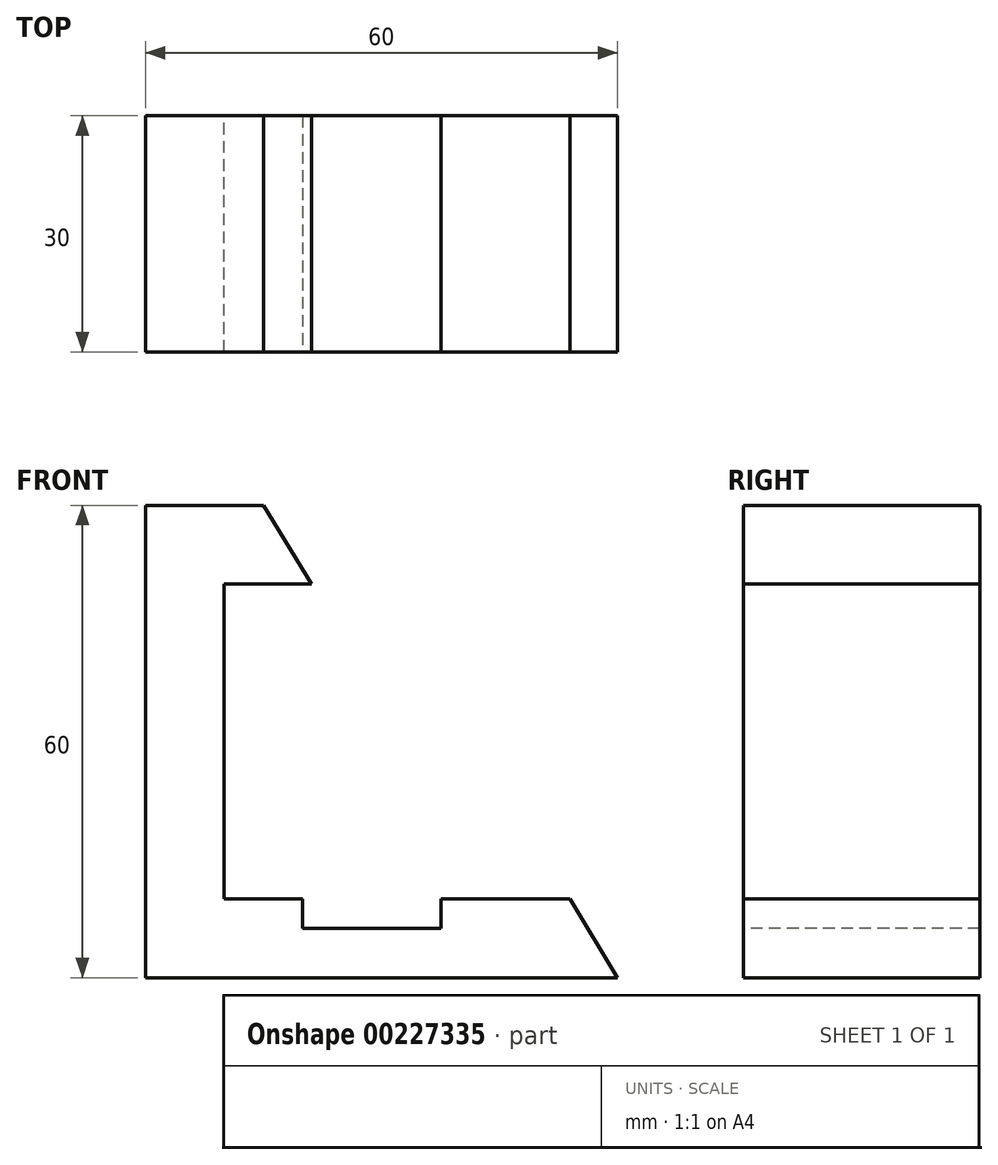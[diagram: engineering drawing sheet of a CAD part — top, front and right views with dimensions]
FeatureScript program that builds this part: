
annotation { "Feature Type Name" : "Feature", "Feature Type Description" : "" }
export const myFeature = defineFeature(function(context is Context, id is Id, definition is map)
    precondition{}
    {
        {
            var Q0;
            Q0=qCreatedBy(makeId("Front.planeOp"),FACE);
            var sketch = newSketch(context, id + "F0", { "sketchPlane" : qUnion([Q0])});
            skLineSegment(sketch, "E0", {"start": v(-68.5, -18.42) * mm, "end": v(-53.5, -18.42) * mm});
            skLineSegment(sketch, "E1", {"start": v(-68.5, -18.42) * mm, "end": v(-68.5, -78.42) * mm});
            skLineSegment(sketch, "E2", {"start": v(-68.5, -78.42) * mm, "end": v(-8.5, -78.42) * mm});
            skPoint(sketch, "E3", {"position": v(-68.5, -40.58) * mm});
            skPoint(sketch, "E4", {"position": v(-58.5, -28.42) * mm});
            skPoint(sketch, "E5", {"position": v(-58.5, -40.48) * mm});
            skLineSegment(sketch, "E6", {"start": v(-58.5, -28.42) * mm, "end": v(-58.5, -40.48) * mm});
            skPoint(sketch, "E7", {"position": v(-58.5, -78.42) * mm});
            skLineSegment(sketch, "E8", {"start": v(-53.5, -18.42) * mm, "end": v(-47.42, -28.42) * mm});
            skLineSegment(sketch, "E9", {"start": v(-58.5, -28.42) * mm, "end": v(-47.42, -28.42) * mm});
            skLineSegment(sketch, "E10", {"start": v(-8.5, -78.42) * mm, "end": v(-14.59, -68.42) * mm});
            skLineSegment(sketch, "E11", {"start": v(-14.59, -68.42) * mm, "end": v(-58.5, -68.42) * mm});
            skLineSegment(sketch, "E12", {"start": v(-58.5, -40.48) * mm, "end": v(-58.5, -68.42) * mm});
            skLineSegment(sketch, "E13", {"start": v(-80, 60) * mm, "end": v(-80, 0) * mm});
            skLineSegment(sketch, "E14", {"start": v(-80, 0) * mm, "end": v(0, 0) * mm});
            skLineSegment(sketch, "E15", {"start": v(-80, 60) * mm, "end": v(-50, 60) * mm});
            skLineSegment(sketch, "E16", {"start": v(-50, 60) * mm, "end": v(-50, 40) * mm});
            skLineSegment(sketch, "E17", {"start": v(-50, 40) * mm, "end": v(-30, 40) * mm});
            skLineSegment(sketch, "E18", {"start": v(-30, 40) * mm, "end": v(-30, 60) * mm});
            skLineSegment(sketch, "E19", {"start": v(-30, 60) * mm, "end": v(0, 60) * mm});
            skLineSegment(sketch, "E20", {"start": v(0, 60) * mm, "end": v(0, 25) * mm});
            skLineSegment(sketch, "E21", {"start": v(0, 25) * mm, "end": v(-10, 25) * mm});
            skLineSegment(sketch, "E22", {"start": v(-10, 25) * mm, "end": v(-10, 15) * mm});
            skLineSegment(sketch, "E23", {"start": v(-10, 15) * mm, "end": v(0, 15) * mm});
            skLineSegment(sketch, "E24", {"start": v(0, 15) * mm, "end": v(0, 0) * mm});
            skSolve(sketch);
        }
        {
            var Q0;
            Q0=makeQuery(id+"F0.imprint","IMPRINT",FACE,{"disambiguationData":[TD([[makeQuery(id+"F0.imprint","IMPRINT",EDGE,{"derivedFrom":sQuery(id+"F0.wireOp",EDGE,"E0")}),-1.0]])]});
            extrude(context, id + "F1", {"entities" : qUnion([Q0]), "depth" : 30 * mm});
        }
        {
            var Q0;
            Q0=makeQuery(id+"F1.opExtrude","CAP_FACE",FACE,{"disambiguationData":[OSD([sQuery(id+"F0.wireOp",EDGE,"E0"),sQuery(id+"F0.wireOp",EDGE,"E1"),sQuery(id+"F0.wireOp",EDGE,"E2"),sQuery(id+"F0.wireOp",EDGE,"E6"),sQuery(id+"F0.wireOp",EDGE,"E8"),sQuery(id+"F0.wireOp",EDGE,"E9"),sQuery(id+"F0.wireOp",EDGE,"E10"),sQuery(id+"F0.wireOp",EDGE,"E11"),sQuery(id+"F0.wireOp",EDGE,"E12")])],"isStart":false});
            var sketch = newSketch(context, id + "F2", { "sketchPlane" : qUnion([Q0])});
            skLineSegment(sketch, "E25.bottom", {"start": v(-48.55, -66.17) * mm, "end": v(-30.95, -66.17) * mm});
            skLineSegment(sketch, "E25.top", {"start": v(-48.55, -72.17) * mm, "end": v(-30.95, -72.17) * mm});
            skLineSegment(sketch, "E25.left", {"start": v(-48.55, -66.17) * mm, "end": v(-48.55, -72.17) * mm});
            skLineSegment(sketch, "E25.right", {"start": v(-30.95, -66.17) * mm, "end": v(-30.95, -72.17) * mm});
            skLineSegment(sketch, "E26.0", {"start": v(-68.5, -18.42) * mm, "end": v(-68.5, -78.42) * mm});
            skLineSegment(sketch, "E27.0", {"start": v(-58.5, -28.42) * mm, "end": v(-58.5, -68.42) * mm});
            skPoint(sketch, "E28.oppositeSnap0", {"position": v(-58.5, -48.42) * mm});
            skLineSegment(sketch, "E28.bottom", {"start": v(-64.92, -40.76) * mm, "end": v(-50.44, -40.76) * mm});
            skLineSegment(sketch, "E28.top", {"start": v(-64.92, -48.42) * mm, "end": v(-50.44, -48.42) * mm});
            skLineSegment(sketch, "E28.left", {"start": v(-64.92, -40.76) * mm, "end": v(-64.92, -48.42) * mm});
            skLineSegment(sketch, "E28.right", {"start": v(-50.44, -40.76) * mm, "end": v(-50.44, -48.42) * mm});
            skSolve(sketch);
        }
        {
            var Q0;
            {var subQ0=sQuery(id+"F2.wireOp",EDGE,"E25.top");Q0=makeQuery(id+"F2.imprint","IMPRINT",FACE,{"disambiguationData":[TD([[makeQuery(id+"F2.imprint","IMPRINT",EDGE,{"derivedFrom":subQ0}),1.0]])]});}
            extrude(context, id + "F3", {"entities" : qUnion([Q0]), "operationType" : NewBodyOperationType.REMOVE, "endBound" : BoundingType.THROUGH_ALL, "oppositeDirection" : true, "depth" : 25 * mm});
        }
    });
